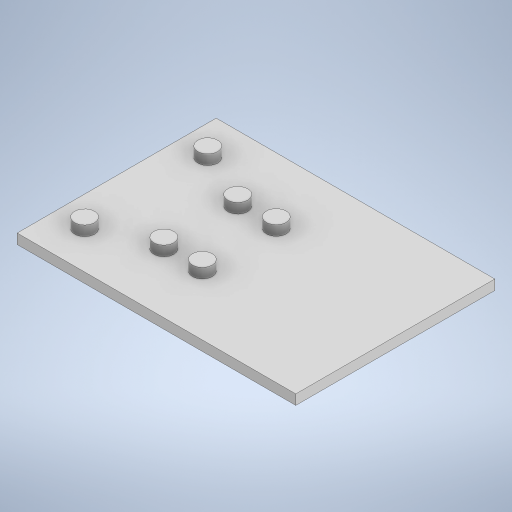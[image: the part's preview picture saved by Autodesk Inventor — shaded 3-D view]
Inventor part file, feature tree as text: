
AUTODESK INVENTOR PART (.ipt)
format: ipt  version: 2024 (Build 280153000, 153)  size: 239,104 bytes
history: native  units: mm
features: extrude x2, sketch x2
ambient origin geometry x8: Origin, YZ Plane, XZ Plane, XY Plane, X Axis, Y Axis, Z Axis, Center Point
bodies: Solid1 (feature_tree)
feature tree (4):
  extrude  "Extrusion1"  Depth=100.0mm
  extrude  "Extrusion2"  Depth=10.0mm
  sketch  "Sketch1"  dims[d0=140.0mm d1=100.0mm]
  sketch  "Sketch2"  dims[d2=5.0mm d3=0.0mm d4=10.0mm d5=10.0mm d6=10.0mm d7=10.0mm d8=10.0mm d9=10.0mm d10=5.0mm d11=0.0mm]
